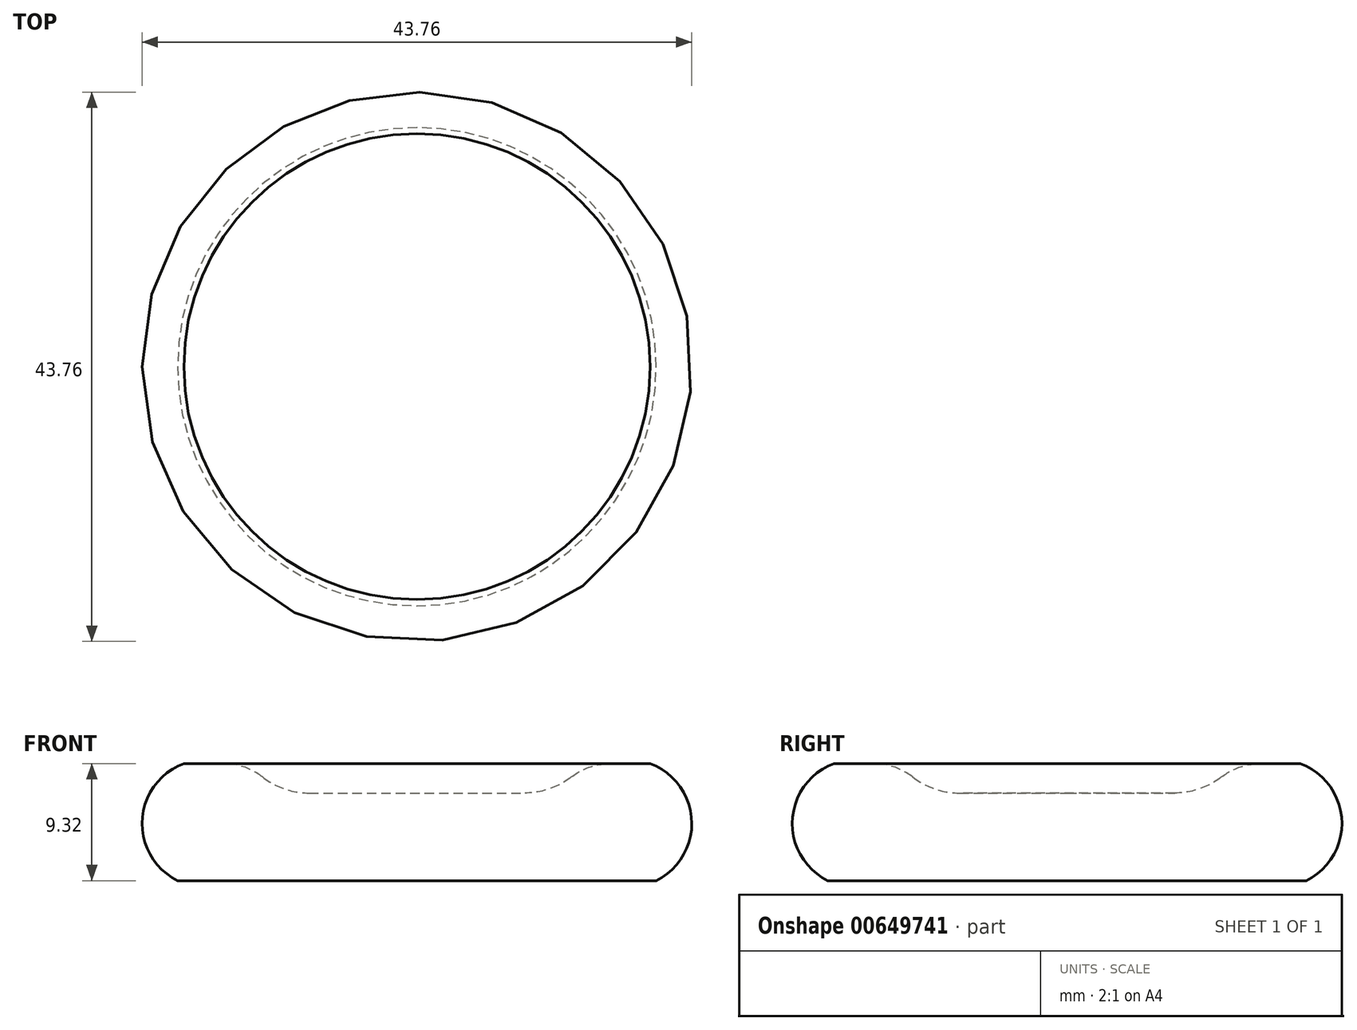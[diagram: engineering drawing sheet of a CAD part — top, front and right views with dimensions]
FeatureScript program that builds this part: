
annotation { "Feature Type Name" : "Feature", "Feature Type Description" : "" }
export const myFeature = defineFeature(function(context is Context, id is Id, definition is map)
    precondition{}
    {
        {
            var Q0;
            Q0=qCreatedBy(makeId("Front.planeOp"),FACE);
            var sketch = newSketch(context, id + "F0", { "sketchPlane" : qUnion([Q0])});
            skLineSegment(sketch, "E0", {"start": v(0, 0) * mm, "end": v(0, 12.7) * mm});
            skLineSegment(sketch, "E1", {"start": v(0, 0) * mm, "end": v(19.05, 0) * mm});
            skArc(sketch, "E2", {"start": v(19.05, 0) * mm, "mid": v(21.87, 4.82) * mm, "end": v(18.56, 9.32) * mm});
            skLineSegment(sketch, "E3", {"start": v(18.56, 9.32) * mm, "end": v(15.37, 9.32) * mm});
            skLineSegment(sketch, "E4", {"start": v(8.59, 6.99) * mm, "end": v(0, 6.99) * mm});
            skArc(sketch, "E5", {"start": v(15.37, 9.32) * mm, "mid": v(13.74, 9.05) * mm, "end": v(12.29, 8.26) * mm});
            skArc(sketch, "E6", {"start": v(8.59, 6.99) * mm, "mid": v(10.54, 7.31) * mm, "end": v(12.29, 8.26) * mm});
            skSolve(sketch);
        }
        {
            var Q0;
            {var subQ0=sQuery(id+"F0.wireOp",EDGE,"E1");Q0=makeQuery(id+"F0.imprint","IMPRINT",FACE,{"disambiguationData":[TD([[makeQuery(id+"F0.imprint","IMPRINT",EDGE,{"derivedFrom":subQ0}),1.0]])]});}
            var Q1;
            Q1=sQuery(id+"F0.wireOp",EDGE,"E0");
            revolve(context, id + "F1", {"entities" : qUnion([Q0]), "axis" : qUnion([Q1]), "revolveType" : RevolveType.FULL});
        }
    });
